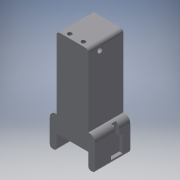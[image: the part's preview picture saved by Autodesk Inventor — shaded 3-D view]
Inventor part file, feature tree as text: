
AUTODESK INVENTOR PART (.ipt)
format: ipt  version: 2016 (Build 200138000, 138)  size: 444,416 bytes
history: native  units: mm
features: extrude x20, sketch x20, fillet x4
ambient origin geometry x8: Origin, YZ Plane, XZ Plane, XY Plane, X Axis, Y Axis, Z Axis, Center Point
bodies: Solid1 (feature_tree)
feature tree (44):
  extrude  "Extrusion1"  Depth=53.0mm
  extrude  "Extrusion2"  Depth=2.0mm
  extrude  "Extrusion3"  Depth=2.0mm
  extrude  "Extrusion4"  Depth=18.0mm TaperAngle=0.0deg
  extrude  "Extrusion5"  Depth=5.0mm
  extrude  "Extrusion7"  Depth=7.5mm
  extrude  "Extrusion9"  Depth=7.5mm TaperAngle=0.0deg
  extrude  "Extrusion8"  Depth=3.5mm TaperAngle=0.0deg
  extrude  "Extrusion10"  Depth=7.3mm
  sketch  "Sketch11"  dims[d35=7.3mm d36=3.5mm d37=0.0mm]
  fillet  "Fillet1"  Radius=2.0mm
  extrude  "Extrusion12"  Depth=18.0mm TaperAngle=0.0deg
  extrude  "Extrusion15"  Depth=12.0mm
  extrude  "Extrusion16"  Depth=8.0mm
  fillet  "Fillet5"  Radius=9.0mm
  extrude  "Extrusion17"  Depth=1.3mm
  extrude  "Extrusion18"  Depth=8.0mm TaperAngle=0.0deg
  extrude  "Extrusion19"  Depth=1.5mm
  extrude  "Extrusion20"  Depth=3.0mm
  extrude  "Extrusion21"  Depth=4.0mm
  extrude  "Extrusion22"  Depth=9.0mm
  fillet  "Fillet6"  Radius=10.0mm
  fillet  "Fillet7"  Radius=4.0mm
  extrude  "Extrusion23"  Depth=3.5mm
  extrude  "Extrusion24"  Depth=10.0mm
  sketch  "Sketch1"  dims[d0=19.0mm d1=53.0mm]
  sketch  "Sketch2"  dims[d2=1.0mm d3=0.0mm d4=2.0mm]
  sketch  "Sketch5"  dims[d5=1.0mm d6=2.0mm]
  sketch  "Sketch6"  dims[d7=1.0mm d8=18.0mm d9=0.0mm]
  sketch  "Sketch7"  dims[d28=5.0mm d29=7.1mm]
  sketch  "Sketch9"  dims[d30=4.5mm d31=7.5mm]
  sketch  "Sketch10"  dims[d32=7.5mm d33=13.0mm d34=0.0mm]
  sketch  "Sketch12"  dims[d38=3.5mm d39=0.0mm d40=7.3mm d46=2.0mm]
  sketch  "Sketch16"  dims[d47=1.0mm d48=18.0mm d49=0.0mm]
  sketch  "Sketch20"  dims[d50=46.0mm d51=0.0mm d52=12.0mm]
  sketch  "Sketch21"  dims[d54=9.0mm d55=8.0mm d57=9.0mm]
  sketch  "Sketch22"  dims[d59=26.0mm d61=1.3mm]
  sketch  "Sketch23"  dims[d62=18.0mm d63=0.0mm d67=8.0mm d68=0.0mm]
  sketch  "Sketch24"  dims[d77=2.0mm d78=1.5mm]
  sketch  "Sketch25"  dims[d79=1.5mm d84=3.0mm]
  sketch  "Sketch28"  dims[d85=7.0mm d86=4.0mm]
  sketch  "Sketch29"  dims[d87=19.0mm d88=0.0mm d106=9.0mm d107=10.0mm d108=4.0mm d109=0.0mm]
  sketch  "Sketch30"  dims[d110=4.0mm d111=0.0mm d112=3.5mm]
  sketch  "Sketch33"  dims[d113=9.0mm d114=10.0mm d121=2.0mm d122=0.0mm d126=3.0mm d127=1.5mm d128=1.5mm d129=5.0mm d130=0.0mm d132=2.0mm d133=3.0mm d137=10.0mm d141=2.0mm d142=0.0mm d143=5.0mm d144=0.0mm d150=2.0mm d151=2.0mm d152=5.5mm d153=1.3mm d154=2.5mm d155=4.0mm d156=3.65mm d157=3.65mm d158=2.5mm d159=3.0mm d160=2.851448mm d161=10.0mm d162=0.0mm d163=2.5mm d164=2.1mm d165=2.1mm d166=1.5mm d167=10.0mm d168=0.0mm d169=0.0mm d170=2.0mm d171=2.0mm d172=1.5mm d180=2.0mm d181=0.0mm d187=0.15mm d189=0.25mm d190=2.0mm d192=4.0mm d193=1.0mm d194=26.3mm d195=0.8mm d196=1.0mm d197=1.0mm d198=18.0mm d199=0.0mm]
